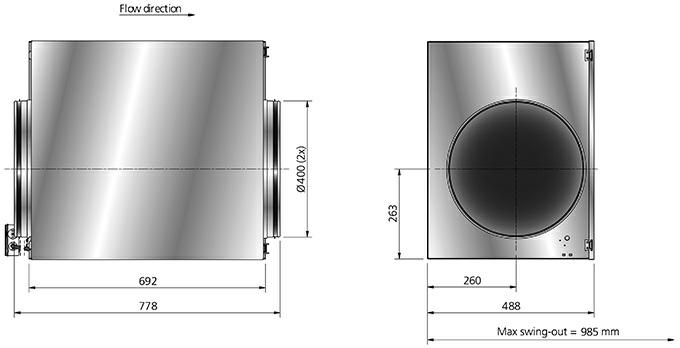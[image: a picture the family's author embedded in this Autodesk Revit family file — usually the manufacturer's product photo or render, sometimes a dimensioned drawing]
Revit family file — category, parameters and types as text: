
# Revit family: IRE 630 A3 ErP AC_
name_source: partatom
category: Mechanical Equipment
revit_build: Autodesk Revit MEP 2014 (Build: 20130308_1515(x64)
units: mm (PartAtom-declared; Revit-internal decimal feet)

## types (1)
- IRE 630 A3 ErP AC
    Capacitor = - μF
    Current = 3 A
    Depth = 955 mm  [stored 3.1332 ft]
    Description = Insulated duct fans with circular connections
    Diameter = 630 mm  [stored 2.06693 ft]
    Frequency = 50 Hz
    Height = 703 mm  [stored 2.30643 ft]
    Main Material = Steel, Galvanized
    Max. temperature of transported air = 60 °C
    Max. temperature of transported air when speed controlled = 60 °C
    Phase = 3
    Power = 1200 W
    Sound pressure level at 3 m = 45 dB(A)
    Speed = 660 rpm
    Voltage = 400 V
    Voltage range = 380-415 V
    Weight = 99.60 kg
    Width = 1067 mm  [stored 3.50066 ft]
    Wiring diagram = Y 4040004 / Δ 4040003

note: [stored X ft] marks values corroborated as IEEE doubles in the binary element streams (Revit-internal decimal feet)

## geometry (parser evidence)
native form markers: Sweep x5
no freeform markers — native parametric forms only
